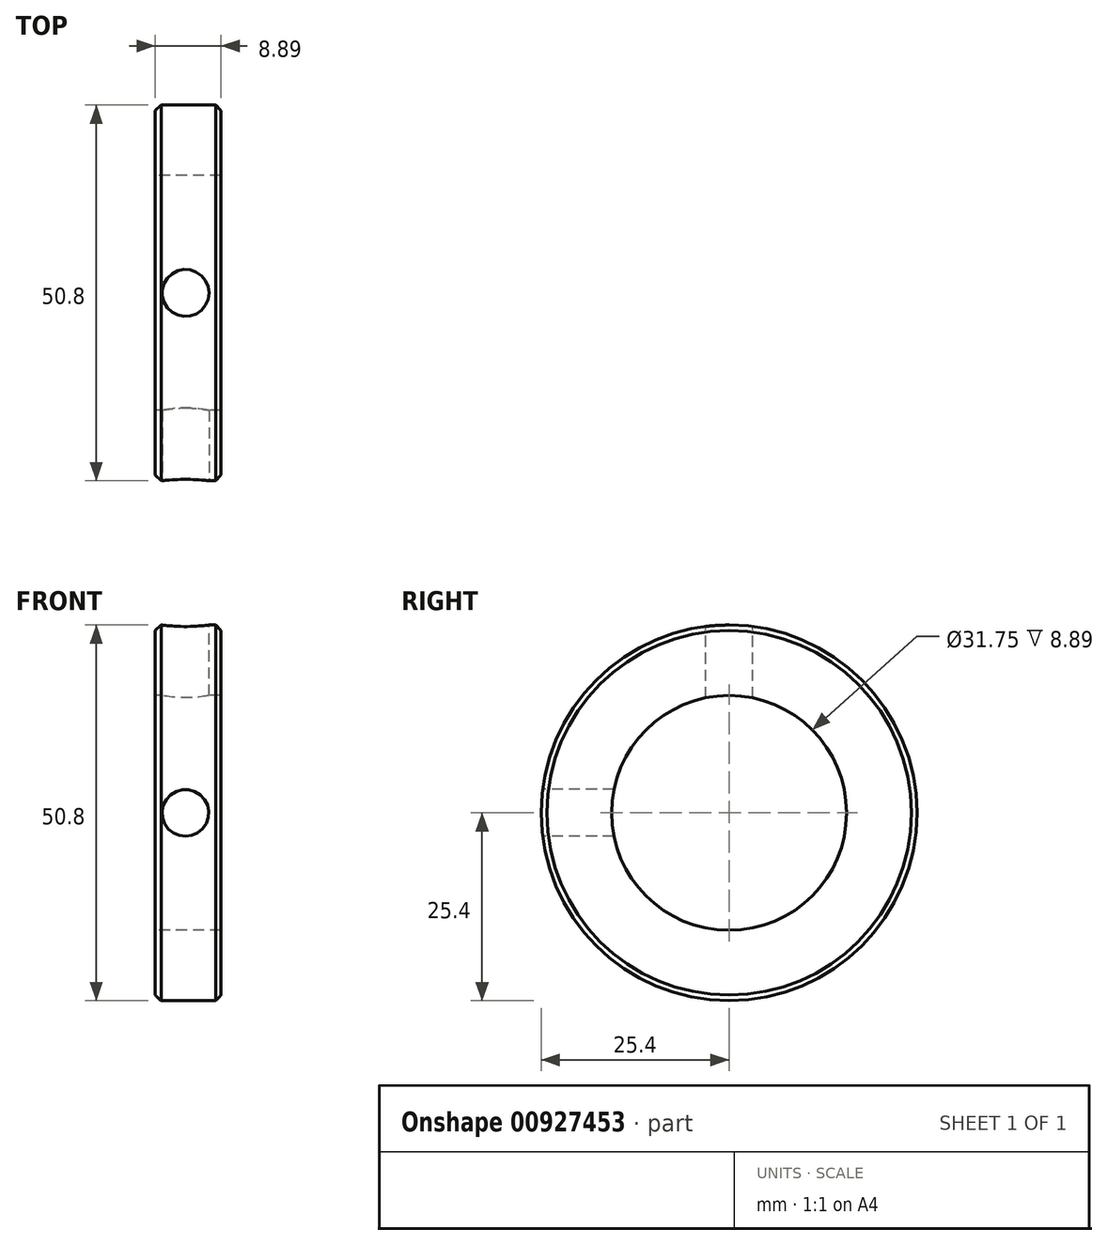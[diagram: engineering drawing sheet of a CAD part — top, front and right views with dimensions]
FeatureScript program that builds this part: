
annotation { "Feature Type Name" : "Feature", "Feature Type Description" : "" }
export const myFeature = defineFeature(function(context is Context, id is Id, definition is map)
    precondition{}
    {
        {
            var Q0;
            Q0=qCreatedBy(makeId("Right.planeOp"),FACE);
            var sketch = newSketch(context, id + "F0", { "sketchPlane" : qUnion([Q0])});
            skCircle(sketch, "E0", {"center": v(0, 0) * mm, "radius": 25.4 * mm});
            skCircle(sketch, "E1", {"center": v(0, 0) * mm, "radius": 15.88 * mm});
            skSolve(sketch);
        }
        {
            var Q0;
            Q0 = qSketchRegion(id + "F0", true);
            extrude(context, id + "F1", {"entities" : qUnion([Q0]), "depth" : 8.9 * mm, "offsetDistance" : 25.4 * mm});
        }
        {
            var Q0;
            Q0=qCreatedBy(makeId("Front.planeOp"),FACE);
            cPlane(context, id + "F2", {"entities" : qUnion([Q0]), "cplaneType" : CPlaneType.OFFSET, "offset" : 25.4 * mm, "width" : 152.4 * mm, "height" : 152.4 * mm});
        }
        {
            var Q0;
            Q0=qCreatedBy(id+"F2.planeOp",FACE);
            var sketch = newSketch(context, id + "F3", { "sketchPlane" : qUnion([Q0])});
            skCircle(sketch, "E2", {"center": v(4.06, 0) * mm, "radius": 3.18 * mm});
            skSolve(sketch);
        }
        {
            var Q0;
            Q0 = qSketchRegion(id + "F3", true);
            var Q1;
            Q1=makeQuery(id+"F1.opExtrude","SWEPT_FACE",FACE,{"disambiguationData":[OSD([sQuery(id+"F0.wireOp",EDGE,"E1")])]});
            extrude(context, id + "F4", {"entities" : qUnion([Q0]), "operationType" : NewBodyOperationType.REMOVE, "endBound" : BoundingType.UP_TO_SURFACE, "oppositeDirection" : true, "depth" : 25.4 * mm, "endBoundEntityFace" : qUnion([Q1]), "offsetDistance" : 25.4 * mm});
        }
        {
            var Q0;
            Q0=qCreatedBy(makeId("Top.planeOp"),FACE);
            cPlane(context, id + "F5", {"entities" : qUnion([Q0]), "cplaneType" : CPlaneType.OFFSET, "offset" : 25.4 * mm, "width" : 152.4 * mm, "height" : 152.4 * mm});
        }
        {
            var Q0;
            Q0=qCreatedBy(id+"F5.planeOp",FACE);
            var sketch = newSketch(context, id + "F6", { "sketchPlane" : qUnion([Q0])});
            skCircle(sketch, "E3", {"center": v(4.06, 0) * mm, "radius": 3.18 * mm});
            skSolve(sketch);
        }
        {
            var Q0;
            Q0 = qSketchRegion(id + "F6", true);
            var Q1;
            Q1=makeQuery(id+"F1.opExtrude","SWEPT_FACE",FACE,{"disambiguationData":[OSD([sQuery(id+"F0.wireOp",EDGE,"E1")])]});
            extrude(context, id + "F7", {"entities" : qUnion([Q0]), "operationType" : NewBodyOperationType.REMOVE, "endBound" : BoundingType.UP_TO_SURFACE, "oppositeDirection" : true, "depth" : 25.4 * mm, "endBoundEntityFace" : qUnion([Q1]), "offsetDistance" : 25.4 * mm});
        }
        {
            var Q0;
            Q0=makeQuery(id+"F1.opExtrude","CAP_EDGE",EDGE,{"disambiguationData":[OSD([sQuery(id+"F0.wireOp",EDGE,"E0")])],"isStart":true});
            chamfer(context, id + "F8", {"entities" : qUnion([Q0]), "width" : 0.76 * mm, "tangentPropagation" : true});
        }
        {
            var Q0;
            Q0=makeQuery(id+"F1.opExtrude","CAP_EDGE",EDGE,{"disambiguationData":[OSD([sQuery(id+"F0.wireOp",EDGE,"E0")])],"isStart":false});
            chamfer(context, id + "F9", {"entities" : qUnion([Q0]), "width" : 0.76 * mm, "tangentPropagation" : true});
        }
    });
